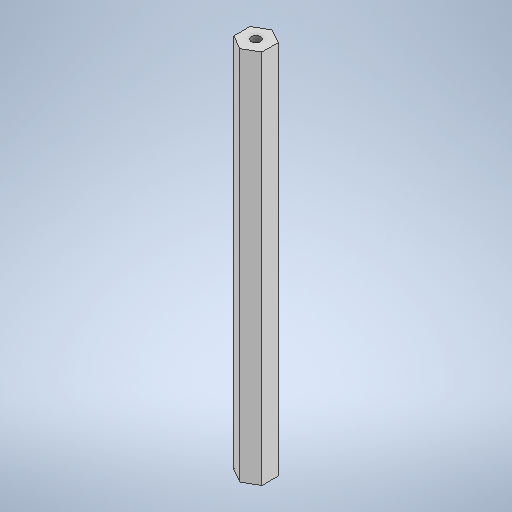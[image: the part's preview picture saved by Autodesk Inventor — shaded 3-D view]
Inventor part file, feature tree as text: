
AUTODESK INVENTOR PART (.ipt)
format: ipt  version: 2025 (Build 290162000, 162)  size: 258,048 bytes
history: native  units: mm
features: sketch x3, other x2, hole x2, extrude x1
ambient origin geometry x8: Origin, YZ Plane, XZ Plane, XY Plane, X Axis, Y Axis, Z Axis, Center Point
bodies: Solid1 (feature_tree)
feature tree (8):
  other  "Annotations"
  extrude  "Extrusion1"  Depth=12.7mm
  hole  "Hole3"  [1 undecoded]
  hole  "Hole4"  [1 undecoded]
  sketch  "Sketch1"  dims[d1=170.0mm d2=0.0mm d19=12.7mm]
  sketch  "Sketch5"  dims[d20=4.134mm d21=10.0mm d22=4.0mm d23=2.0mm d24=90.0deg d25=14.2mm d26=20.594885mm]
  sketch  "Sketch6"  dims[d27=4.134mm d28=10.0mm d29=4.0mm d30=2.0mm d31=90.0deg d32=14.2mm d33=20.594885mm]
  other  "General Note 1"
note: 2 required parameter values undecoded (feature->parameter linkage not recoverable at this tier; creation-order binding heuristic only, values carry confidence <= 0.55)
